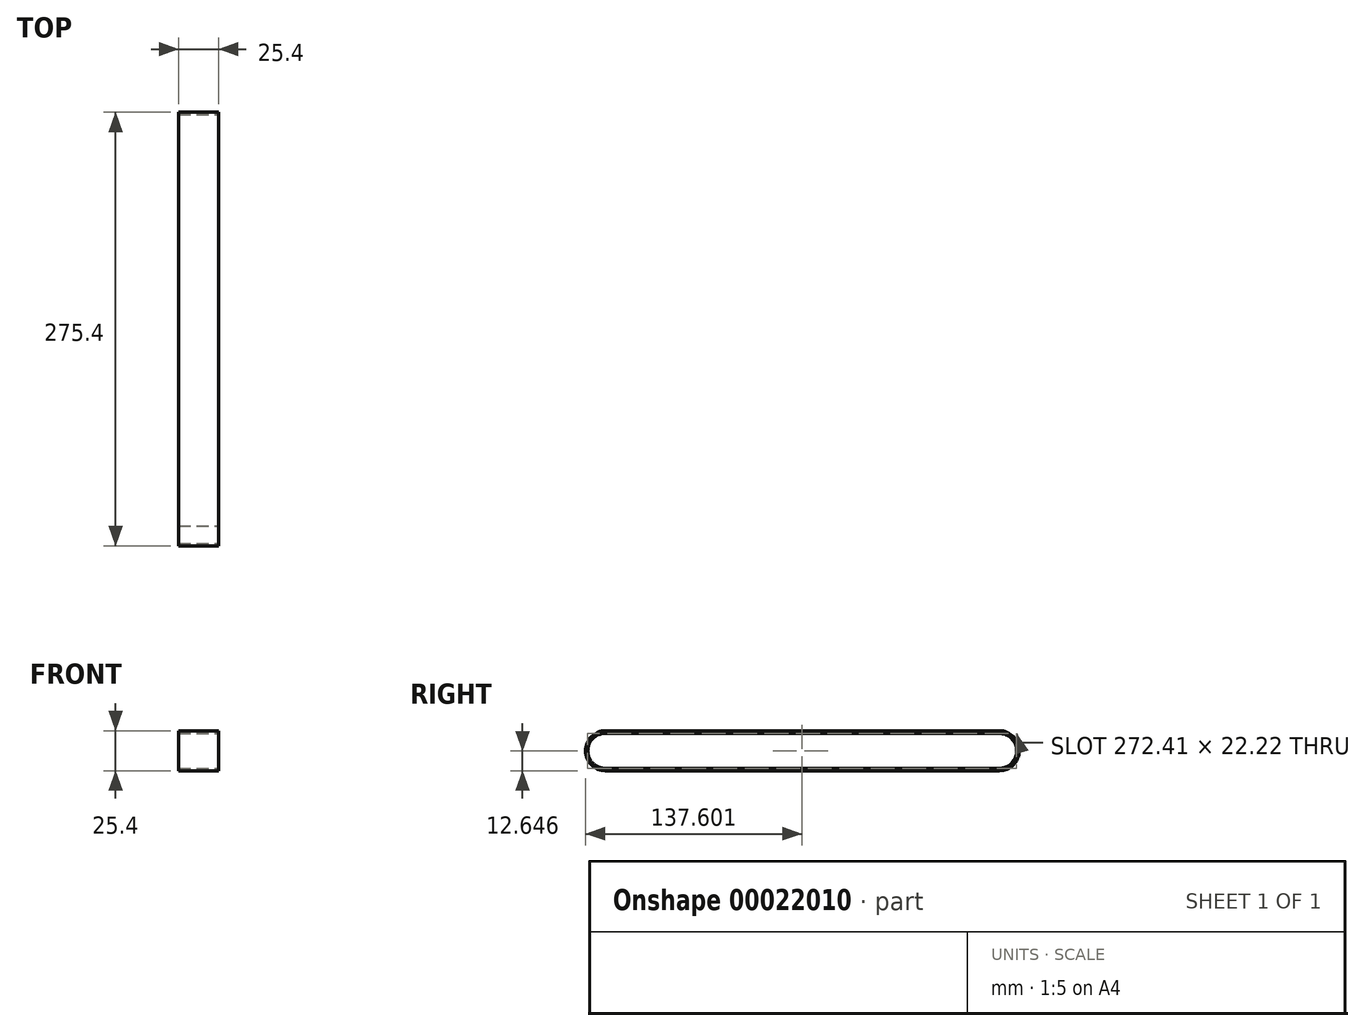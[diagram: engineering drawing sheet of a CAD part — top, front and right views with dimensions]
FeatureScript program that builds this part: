
annotation { "Feature Type Name" : "Feature", "Feature Type Description" : "" }
export const myFeature = defineFeature(function(context is Context, id is Id, definition is map)
    precondition{}
    {
        {
            var Q0;
            Q0=qCreatedBy(makeId("Right.planeOp"),FACE);
            var sketch = newSketch(context, id + "F0", { "sketchPlane" : qUnion([Q0])});
            skLineSegment(sketch, "E0", {"start": v(-48.04, 47.02) * mm, "end": v(201.96, 47.02) * mm});
            skLineSegment(sketch, "E1", {"start": v(-48.04, 21.62) * mm, "end": v(201.96, 21.62) * mm});
            skArc(sketch, "E2", {"start": v(201.96, 21.62) * mm, "mid": v(214.66, 34.32) * mm, "end": v(201.96, 47.02) * mm});
            skLineSegment(sketch, "E3", {"start": v(-48.04, 47.02) * mm, "end": v(-48.04, 21.62) * mm});
            skLineSegment(sketch, "E4", {"start": v(201.96, 47.02) * mm, "end": v(201.96, 21.62) * mm});
            skArc(sketch, "E5", {"start": v(-48.04, 47.02) * mm, "mid": v(-60.74, 34.32) * mm, "end": v(-48.04, 21.62) * mm});
            skSolve(sketch);
        }
        {
            var Q0;
            Q0=makeQuery(id+"F0.imprint","IMPRINT",FACE,{"disambiguationData":[TD([[makeQuery(id+"F0.imprint","IMPRINT",EDGE,{"derivedFrom":sQuery(id+"F0.wireOp",EDGE,"E0")}),-1.0]])]});
            var Q1;
            Q1=makeQuery(id+"F0.imprint","IMPRINT",FACE,{"disambiguationData":[TD([[makeQuery(id+"F0.imprint","IMPRINT",EDGE,{"derivedFrom":sQuery(id+"F0.wireOp",EDGE,"E2")}),1.0]])]});
            var Q2;
            Q2=makeQuery(id+"F0.imprint","IMPRINT",FACE,{"disambiguationData":[TD([[makeQuery(id+"F0.imprint","IMPRINT",EDGE,{"derivedFrom":sQuery(id+"F0.wireOp",EDGE,"E3")}),-1.0]])]});
            extrude(context, id + "F1", {"entities" : qUnion([Q0, Q1, Q2]), "depth" : 25.4 * mm});
        }
        {
            var Q0;
            Q0=makeQuery(id+"F1.opExtrude","CAP_FACE",FACE,{"disambiguationData":[OSD([sQuery(id+"F0.wireOp",EDGE,"E0"),sQuery(id+"F0.wireOp",EDGE,"E1"),sQuery(id+"F0.wireOp",EDGE,"E2"),sQuery(id+"F0.wireOp",EDGE,"E5")])],"isStart":false});
            var sketch = newSketch(context, id + "F2", { "sketchPlane" : qUnion([Q0])});
            skLineSegment(sketch, "E6", {"start": v(-48.04, 47.02) * mm, "end": v(-48.04, 21.62) * mm});
            skLineSegment(sketch, "E7", {"start": v(201.96, 47.02) * mm, "end": v(201.96, 21.62) * mm});
            skLineSegment(sketch, "E8", {"start": v(-48.04, 47.02) * mm, "end": v(201.96, 47.02) * mm});
            skLineSegment(sketch, "E9", {"start": v(-48.04, 21.62) * mm, "end": v(201.96, 21.62) * mm});
            skArc(sketch, "E10", {"start": v(-48.04, 45.38) * mm, "mid": v(-59.35, 34.27) * mm, "end": v(-48.04, 23.16) * mm});
            skLineSegment(sketch, "E11", {"start": v(-48.04, 23.16) * mm, "end": v(201.96, 23.16) * mm});
            skLineSegment(sketch, "E12", {"start": v(-48.04, 45.38) * mm, "end": v(201.96, 45.38) * mm});
            skArc(sketch, "E13", {"start": v(201.96, 23.16) * mm, "mid": v(213.07, 34.27) * mm, "end": v(201.96, 45.38) * mm});
            skSolve(sketch);
        }
        {
            var Q0;
            {var subQ0=sQuery(id+"F2.wireOp",EDGE,"E10");Q0=makeQuery(id+"F2.imprint","IMPRINT",FACE,{"disambiguationData":[TD([[makeQuery(id+"F2.imprint","IMPRINT",EDGE,{"derivedFrom":subQ0}),1.0]])]});}
            var Q1;
            {var subQ1=sQuery(id+"F2.wireOp",EDGE,"E11");Q1=makeQuery(id+"F2.imprint","IMPRINT",FACE,{"disambiguationData":[TD([[makeQuery(id+"F2.imprint","IMPRINT",EDGE,{"derivedFrom":subQ1}),1.0]])]});}
            var Q2;
            {var subQ0=sQuery(id+"F2.wireOp",EDGE,"E13");Q2=makeQuery(id+"F2.imprint","IMPRINT",FACE,{"disambiguationData":[TD([[makeQuery(id+"F2.imprint","IMPRINT",EDGE,{"derivedFrom":subQ0}),1.0]])]});}
            extrude(context, id + "F3", {"entities" : qUnion([Q0, Q1, Q2]), "operationType" : NewBodyOperationType.REMOVE, "oppositeDirection" : true, "depth" : 25.4 * mm});
        }
    });
